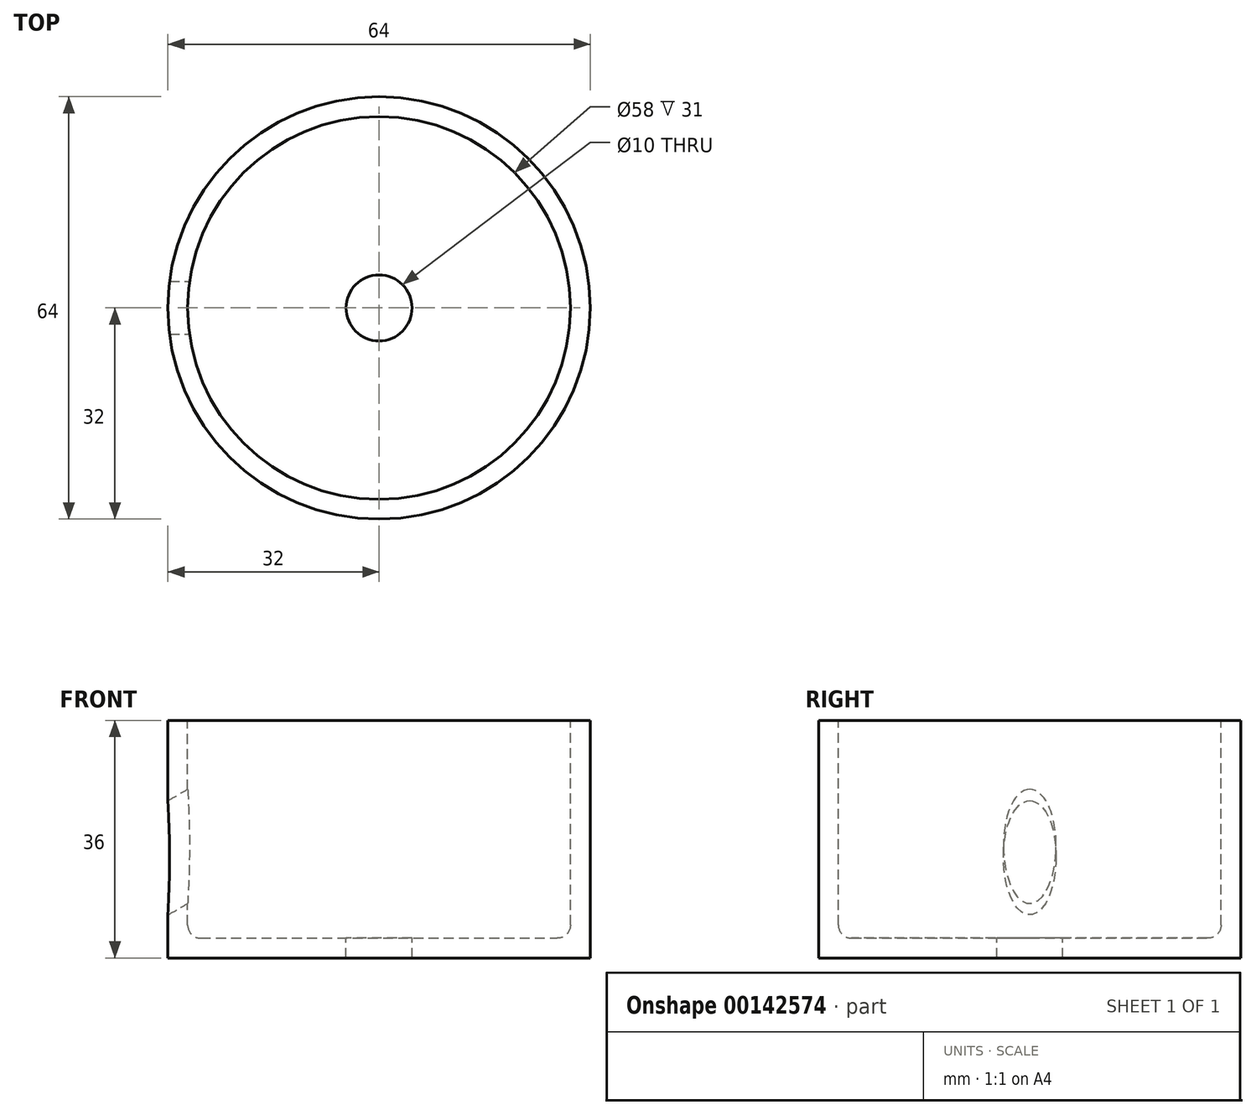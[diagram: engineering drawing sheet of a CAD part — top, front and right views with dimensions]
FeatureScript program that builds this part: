
annotation { "Feature Type Name" : "Feature", "Feature Type Description" : "" }
export const myFeature = defineFeature(function(context is Context, id is Id, definition is map)
    precondition{}
    {
        {
            var Q0;
            Q0=qCreatedBy(makeId("Front.planeOp"),FACE);
            var sketch = newSketch(context, id + "F0", { "sketchPlane" : qUnion([Q0])});
            skLineSegment(sketch, "E0", {"start": v(0, 0) * mm, "end": v(-32, 0) * mm});
            skLineSegment(sketch, "E1", {"start": v(-32, 0) * mm, "end": v(-32, 36) * mm});
            skLineSegment(sketch, "E2", {"start": v(-32, 36) * mm, "end": v(-29, 36) * mm});
            skLineSegment(sketch, "E3", {"start": v(-29, 36) * mm, "end": v(-29, 3) * mm});
            skLineSegment(sketch, "E4", {"start": v(-29, 3) * mm, "end": v(0, 3) * mm});
            skLineSegment(sketch, "E5", {"start": v(0, 3) * mm, "end": v(0, 0) * mm});
            skSolve(sketch);
        }
        {
            var Q0;
            Q0=makeQuery(id+"F0.imprint","IMPRINT",FACE,{"disambiguationData":[TD([[makeQuery(id+"F0.imprint","IMPRINT",EDGE,{"derivedFrom":sQuery(id+"F0.wireOp",EDGE,"E0")}),-1.0]])]});
            var Q1;
            Q1=sQuery(id+"F0.wireOp",EDGE,"E5");
            revolve(context, id + "F1", {"entities" : qUnion([Q0]), "axis" : qUnion([Q1]), "revolveType" : RevolveType.FULL});
        }
        {
            var Q0;
            Q0=makeQuery(id+"F1.opRevolve","SWEPT_EDGE",EDGE,{"disambiguationData":[OSD([sQuery(id+"F0.wireOp",EDGE,"E3"),sQuery(id+"F0.wireOp",EDGE,"E4")])]});
            fillet(context, id + "F2", {"entities" : qUnion([Q0]), "radius" : 2 * mm, "tangentPropagation" : true, "allowEdgeOverflow" : false});
        }
        {
            var Q0;
            Q0=makeQuery(id+"F1.opRevolve","SWEPT_FACE",FACE,{"disambiguationData":[OSD([sQuery(id+"F0.wireOp",EDGE,"E4")])]});
            var sketch = newSketch(context, id + "F3", { "sketchPlane" : qUnion([Q0])});
            skCircle(sketch, "E6", {"center": v(0, 0) * mm, "radius": 5 * mm});
            skSolve(sketch);
        }
        {
            var Q0;
            Q0=makeQuery(id+"F3.imprint","IMPRINT",FACE,{"disambiguationData":[TD([[makeQuery(id+"F3.imprint","IMPRINT",EDGE,{"derivedFrom":sQuery(id+"F3.wireOp",EDGE,"E6")}),1.0]])]});
            extrude(context, id + "F4", {"entities" : qUnion([Q0]), "operationType" : NewBodyOperationType.REMOVE, "endBound" : BoundingType.THROUGH_ALL, "oppositeDirection" : true, "depth" : 25 * mm});
        }
        {
            var Q0;
            Q0=qCreatedBy(makeId("Top.planeOp"),FACE);
            var sketch = newSketch(context, id + "F5", { "sketchPlane" : qUnion([Q0])});
            skLineSegment(sketch, "E7", {"start": v(0, 50.78) * mm, "end": v(0, -54.95) * mm});
            skSolve(sketch);
        }
        {
            var Q0;
            Q0=sQuery(id+"F5.wireOp",EDGE,"E7");
            var Q1;
            Q1=qCreatedBy(makeId("Right.planeOp"),FACE);
            cPlane(context, id + "F6", {"entities" : qUnion([Q0, Q1]), "cplaneType" : CPlaneType.LINE_ANGLE, "offset" : 25 * mm, "angle" : 30 * degree, "width" : 150 * mm, "height" : 150 * mm});
        }
        {
            var Q0;
            Q0=qCreatedBy(id+"F6.planeOp",FACE);
            var sketch = newSketch(context, id + "F7", { "sketchPlane" : qUnion([Q0])});
            skEllipse(sketch, "E8", {"center": v(0, 29.13) * mm, "majorRadius": 7.5 * mm, "minorRadius": 4 * mm, "majorAxis": v(0, 1)});
            skSolve(sketch);
        }
        {
            var Q0;
            Q0=makeQuery(id+"F7.imprint","IMPRINT",FACE,{"disambiguationData":[TD([[makeQuery(id+"F7.imprint","IMPRINT",EDGE,{"derivedFrom":sQuery(id+"F7.wireOp",EDGE,"E8")}),1.0]])]});
            extrude(context, id + "F8", {"entities" : qUnion([Q0]), "operationType" : NewBodyOperationType.REMOVE, "endBound" : BoundingType.THROUGH_ALL, "depth" : 25 * mm});
        }
    });
